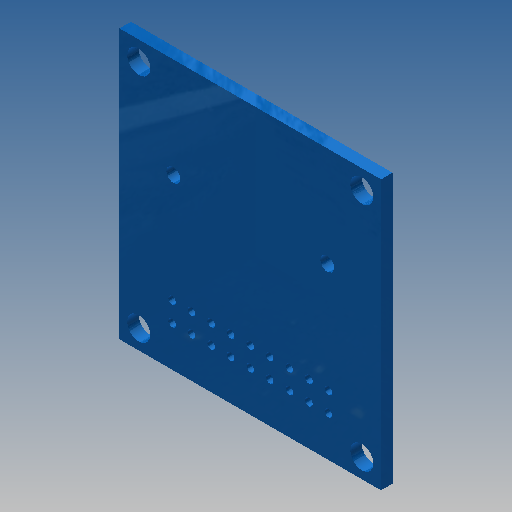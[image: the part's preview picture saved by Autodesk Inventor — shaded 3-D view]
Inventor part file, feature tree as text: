
AUTODESK INVENTOR PART (.ipt)
format: ipt  version: 2020 (Build 240168000, 168)  size: 139,264 bytes
history: native  units: mm
features: other x1, hole x1
ambient origin geometry x8: Origin, YZ Plane, XZ Plane, XY Plane, X Axis, Y Axis, Z Axis, Center Point
bodies: Body1 (feature_tree)
feature tree (2):
  other  "Твердое тело1"
  hole  "Holes"  [1 undecoded]
note: 1 required parameter value undecoded (feature->parameter linkage not recoverable at this tier; creation-order binding heuristic only, values carry confidence <= 0.55)
